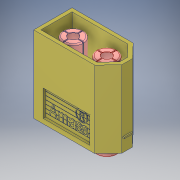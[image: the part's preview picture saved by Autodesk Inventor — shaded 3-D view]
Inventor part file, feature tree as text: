
AUTODESK INVENTOR PART (.ipt)
format: ipt  version: 2019 (Build 230136000, 136)  size: 912,384 bytes
history: mixed  units: in
note: dims shown in document units (in); Inventor stores cm internally (conversion verified against a paired STEP export)
features: fillet x2, imported_body x1
ambient origin geometry x8: Origin, YZ Plane, XZ Plane, XY Plane, X Axis, Y Axis, Z Axis, Center Point
bodies: Solid1 (imported_parasolid), Solid2 (imported_parasolid)
feature tree (3):
  fillet  "Fillet6"  [1 undecoded]
  fillet  "Fillet7"  [1 undecoded]
  imported_body  NMx_Import_Brep_tag  [imported B-rep: ~18 faces, bbox_mm=[10.741657, 0.0, 1.745829]]
note: 2 required parameter values undecoded (feature->parameter linkage not recoverable at this tier; creation-order binding heuristic only, values carry confidence <= 0.55)
